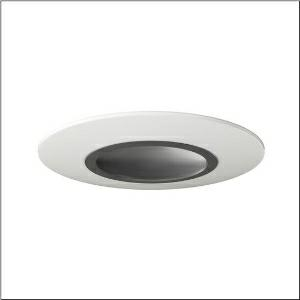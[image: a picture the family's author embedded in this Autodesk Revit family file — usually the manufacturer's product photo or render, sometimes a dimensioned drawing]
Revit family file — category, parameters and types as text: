
# Revit family: rondel_21_0md5307l1840
name_source: partatom
category: Lighting Fixtures
units: mm (PartAtom-declared; Revit-internal decimal feet)

## family parameters
Cut with Voids When Loaded = No
Host = Face
Light Source = No
Part Type = Normal
Room Calculation Point = No
Round Connector Dimension = Use Diameter
Shared = No

## types (1)
- Rondel 21 (1 x LED 4000K / CRI = 80 (unbekannt), 1800 lm, 4000K)
    Apparent Load = 18 VA
    CIE Flux Codes = 43 74 92 91 100
    Color Rendering = 80
    Color Temperature = 4000K
    Default Elevation = 1800 mm  [stored 5.90551 ft]
    Description = Rondel 21, wall and ceiling luminaire, of PC, opal, light emission: direct distribution, installation type: surface-mounted, LED rated luminous flux: 1.800 lm, light colour: 840, colour temperature: 4000K, control gear: ECG, with terminal, 2-pole, mains connection: 220..240V, AC, 50/60Hz, rated input power: 18W, housing, round, of sheet steel, powder-coated, white, diameter: 380 mm, height: 28mm, cover, of PC, graphite (RAL 7037), protection rating (complete): IP40, insulation class (complete): insulation class II (safety insulation), certification: CE, impact resistance: IK03, permissible ambient temperature for indoor applications: -20..+40°C, permissible storage temperature: -20..+80°C, packaging unit: 1 piece
    Height = 28 mm
    Lamp = 1 x LED 4000K / CRI >= 80 (unbekannt)
    Lamp Light Flux = 1800 lm
    Lamp count = 1
    Length = 380 mm
    Luminous efficacy = 100 lm/W
    Manufacturer = Siteco
    ModVariant = No
    Model = 0MD5307L1840
    Mounting Place = Ceiling
    Mounting Type = Surface mounted
    Number of Poles = 1
    OnlyDefault = Yes
    Power Factor = 1
    Product Name = Rondel 21
    Product group = wall and ceiling luminaire
    ProductGroupID = 301
    Protection Class = Protection class II
    Protection Degree = IP 40
    RLX_Detail_Level = 1
    RlxData = <blob elided: 61501 chars, md5=778bde22>
    Socket = socket
    Standby Power = 0 W
    System Light Flux = 1800 lm
    System Power = 18 W
    Type Comments = Product without accessories
    Type Image = l_1005688.jpg
    URL = http://relux.com
    VarID = ---
    Voltage = 0 V
    Weight = 0.00 kg
    Width = 0 mm  [stored 0 ft]

note: [stored X ft] marks values corroborated as IEEE doubles in the binary element streams (Revit-internal decimal feet)

## geometry (parser evidence)
native form markers: Blend x4, Sweep x13
no freeform markers — native parametric forms only
